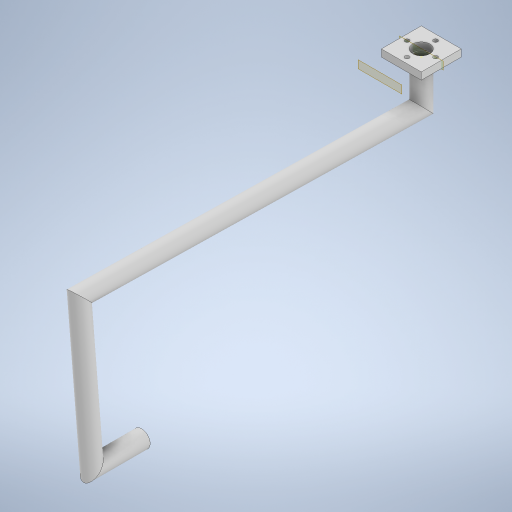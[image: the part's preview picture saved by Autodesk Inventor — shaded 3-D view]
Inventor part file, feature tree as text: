
AUTODESK INVENTOR PART (.ipt)
format: ipt  version: 2023 (Build 270158000, 158)  size: 310,272 bytes
history: native  units: mm
features: sketch x6, extrude x2, plane x2, sweep x1, chamfer x1
ambient origin geometry x8: Origin, YZ Plane, XZ Plane, XY Plane, X Axis, Y Axis, Z Axis, Center Point
bodies: Solid1 (feature_tree)
feature tree (12):
  extrude  "Extrusion1"  Depth=28.0mm
  extrude  "Extrusion2"  Depth=14.0mm
  plane  "Work Plane1"
  sketch  "Sketch3"  dims[d4=5.0mm d5=0.0mm d6=12.0mm]
  sketch  "3D Sketch1"
  sketch  "3D Sketch2"
  sweep  "Sweep1"
  chamfer  "Chamfer1"  Distance=10.0mm
  plane  "Work Plane2"
  sketch  "Sketch1"  dims[d0=28.0mm d1=28.0mm]
  sketch  "Sketch2"  dims[d2=14.0mm d3=14.0mm]
  sketch  "Sketch4"  dims[d7=3.0mm d8=10.0mm d9=40.0mm d11=360.0deg d13=5.0mm d14=0.0mm d15=-14.0mm d16=30.0mm d19=10.0mm d20=0.0mm d21=0.0mm d22=12.0mm d23=1.0mm d24=2.0mm d25=45.0deg d44=15.0mm d53=100.0mm d54=14.835299mm d55=35.0mm d56=240.0mm d57=90.0deg d58=90.0deg d29=0.0mm d30=0.0mm d31=0.0mm d32=0.0mm]
